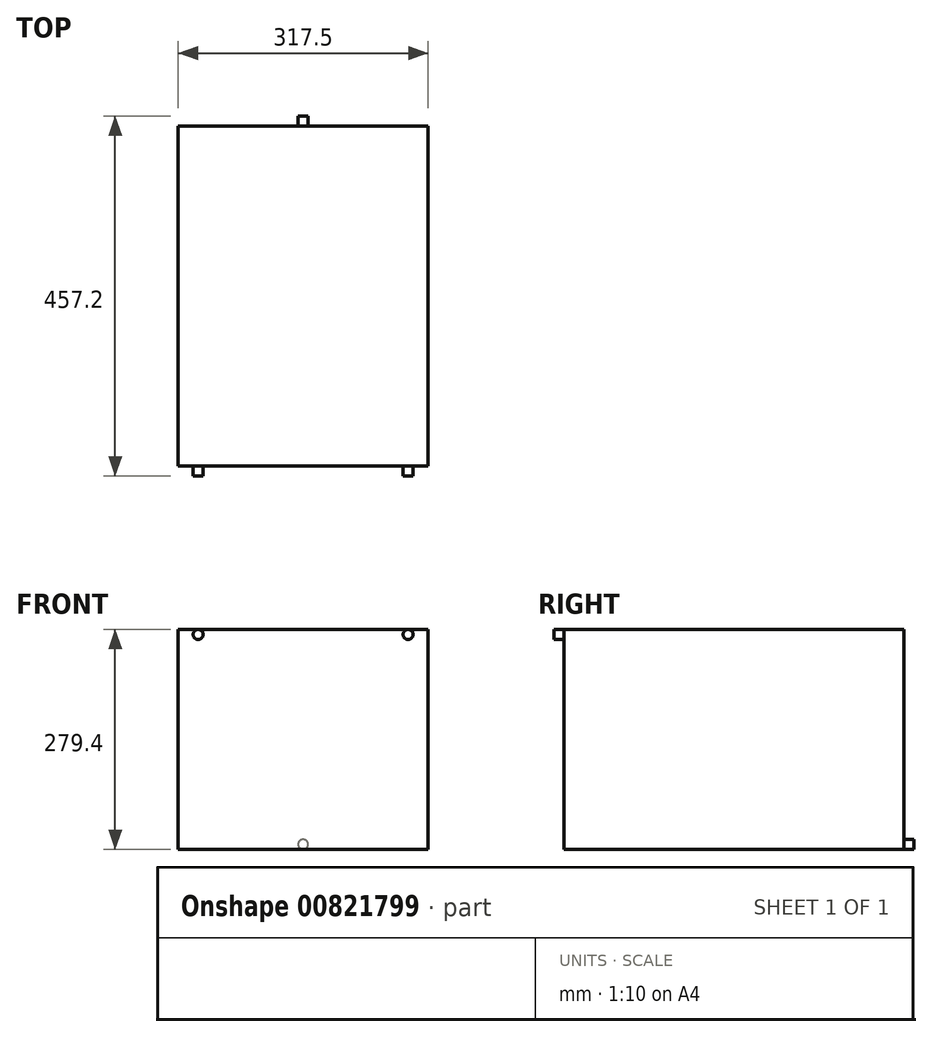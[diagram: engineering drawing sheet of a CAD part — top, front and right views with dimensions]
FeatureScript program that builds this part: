
annotation { "Feature Type Name" : "Feature", "Feature Type Description" : "" }
export const myFeature = defineFeature(function(context is Context, id is Id, definition is map)
    precondition{}
    {
        {
            var Q0;
            Q0=qCreatedBy(makeId("Top.planeOp"),FACE);
            var sketch = newSketch(context, id + "F0", { "sketchPlane" : qUnion([Q0])});
            skLineSegment(sketch, "E0", {"start": v(0, 0) * mm, "end": v(-317.5, 0) * mm});
            skLineSegment(sketch, "E1", {"start": v(0, 0) * mm, "end": v(0, 431.8) * mm});
            skLineSegment(sketch, "E2", {"start": v(0, 431.8) * mm, "end": v(-317.5, 431.8) * mm});
            skLineSegment(sketch, "E3", {"start": v(-317.5, 431.8) * mm, "end": v(-317.5, 0) * mm});
            skSolve(sketch);
        }
        {
            var Q0;
            Q0 = qSketchRegion(id + "F0", true);
            extrude(context, id + "F1", {"entities" : qUnion([Q0]), "depth" : 279.4 * mm, "offsetDistance" : 25.4 * mm});
        }
        {
            var Q0;
            Q0=makeQuery(id+"F1.opExtrude","SWEPT_FACE",FACE,{"disambiguationData":[OSD([sQuery(id+"F0.wireOp",EDGE,"E2")])]});
            var sketch = newSketch(context, id + "F2", { "sketchPlane" : qUnion([Q0])});
            skCircle(sketch, "E4", {"center": v(158.75, 6.35) * mm, "radius": 6.35 * mm});
            skPoint(sketch, "E4.centerSnap0", {"position": v(158.75, 0) * mm});
            skSolve(sketch);
        }
        {
            var Q0;
            Q0 = qSketchRegion(id + "F2", true);
            extrude(context, id + "F3", {"entities" : qUnion([Q0]), "operationType" : NewBodyOperationType.ADD, "depth" : 12.7 * mm, "offsetDistance" : 25.4 * mm});
        }
        {
            var Q0;
            Q0=makeQuery(id+"F1.opExtrude","SWEPT_FACE",FACE,{"disambiguationData":[OSD([sQuery(id+"F0.wireOp",EDGE,"E0")])]});
            var sketch = newSketch(context, id + "F4", { "sketchPlane" : qUnion([Q0])});
            skLineSegment(sketch, "E5", {"start": v(-317.5, 273.05) * mm, "end": v(-292.1, 273.05) * mm});
            skLineSegment(sketch, "E6", {"start": v(0, 273.05) * mm, "end": v(-25.4, 273.05) * mm});
            skCircle(sketch, "E7", {"center": v(-292.1, 273.05) * mm, "radius": 6.35 * mm});
            skCircle(sketch, "E8", {"center": v(-25.4, 273.05) * mm, "radius": 6.35 * mm});
            skSolve(sketch);
        }
        {
            var Q0;
            Q0 = qSketchRegion(id + "F4", true);
            extrude(context, id + "F5", {"entities" : qUnion([Q0]), "operationType" : NewBodyOperationType.ADD, "depth" : 12.7 * mm, "offsetDistance" : 25.4 * mm});
        }
    });
